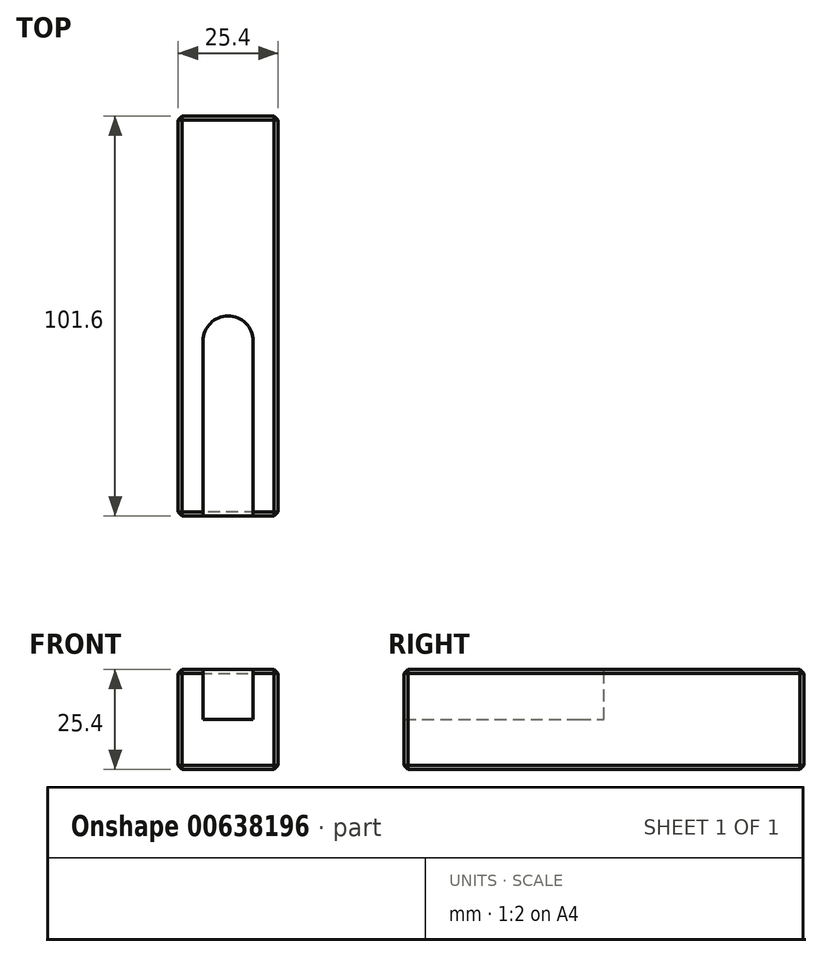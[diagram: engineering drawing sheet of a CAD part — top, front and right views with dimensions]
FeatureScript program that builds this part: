
annotation { "Feature Type Name" : "Feature", "Feature Type Description" : "" }
export const myFeature = defineFeature(function(context is Context, id is Id, definition is map)
    precondition{}
    {
        {
            var Q0;
            Q0=qCreatedBy(makeId("Front.planeOp"),FACE);
            var sketch = newSketch(context, id + "F0", { "sketchPlane" : qUnion([Q0])});
            skLineSegment(sketch, "E0.bottom", {"start": v(12.7, -12.7) * mm, "end": v(-12.7, -12.7) * mm});
            skLineSegment(sketch, "E0.top", {"start": v(12.7, 12.7) * mm, "end": v(-12.7, 12.7) * mm});
            skLineSegment(sketch, "E0.left", {"start": v(12.7, -12.7) * mm, "end": v(12.7, 12.7) * mm});
            skLineSegment(sketch, "E0.right", {"start": v(-12.7, -12.7) * mm, "end": v(-12.7, 12.7) * mm});
            skPoint(sketch, "E0.middle", {"position": v(0, 0) * mm});
            skSolve(sketch);
        }
        {
            var Q0;
            Q0=makeQuery(id+"F0.imprint","IMPRINT",FACE,{"disambiguationData":[TD([[makeQuery(id+"F0.imprint","IMPRINT",EDGE,{"derivedFrom":sQuery(id+"F0.wireOp",EDGE,"E0.bottom")}),-1.0]])]});
            extrude(context, id + "F1", {"entities" : qUnion([Q0]), "endBound" : BoundingType.SYMMETRIC, "depth" : (25.4 * 4) * mm, "offsetDistance" : 25 * mm});
        }
        {
            var Q0;
            Q0=makeQuery(id+"F1.opExtrude","SWEPT_FACE",FACE,{"disambiguationData":[OSD([sQuery(id+"F0.wireOp",EDGE,"E0.top")])]});
            var sketch = newSketch(context, id + "F2", { "sketchPlane" : qUnion([Q0])});
            skLineSegment(sketch, "E1.bottom", {"start": v(-6.35, -50.8) * mm, "end": v(6.35, -50.8) * mm});
            skLineSegment(sketch, "E1.left", {"start": v(-6.35, -50.8) * mm, "end": v(-6.35, -6.35) * mm});
            skLineSegment(sketch, "E1.right", {"start": v(6.35, -50.8) * mm, "end": v(6.35, -6.35) * mm});
            skArc(sketch, "E2", {"start": v(6.35, -6.35) * mm, "mid": v(0, 0) * mm, "end": v(-6.35, -6.35) * mm});
            skSolve(sketch);
        }
        {
            var Q0;
            Q0=makeQuery(id+"F2.imprint","IMPRINT",FACE,{"disambiguationData":[TD([[makeQuery(id+"F2.imprint","IMPRINT",EDGE,{"derivedFrom":sQuery(id+"F2.wireOp",EDGE,"E1.bottom")}),-1.0]])]});
            extrude(context, id + "F3", {"entities" : qUnion([Q0]), "operationType" : NewBodyOperationType.REMOVE, "oppositeDirection" : true, "depth" : (25.4 / 2) * mm, "offsetDistance" : 25 * mm});
        }
        {
            var Q0;
            Q0=makeQuery(id+"F1.opExtrude","SWEPT_FACE",FACE,{"disambiguationData":[OSD([sQuery(id+"F0.wireOp",EDGE,"E0.left")])]});
            var Q1;
            Q1=makeQuery(id+"F1.opExtrude","CAP_FACE",FACE,{"disambiguationData":[OSD([sQuery(id+"F0.wireOp",EDGE,"E0.bottom"),sQuery(id+"F0.wireOp",EDGE,"E0.top"),sQuery(id+"F0.wireOp",EDGE,"E0.left"),sQuery(id+"F0.wireOp",EDGE,"E0.right")])],"isStart":true});
            var Q2;
            Q2=makeQuery(id+"F1.opExtrude","SWEPT_FACE",FACE,{"disambiguationData":[OSD([sQuery(id+"F0.wireOp",EDGE,"E0.right")])]});
            var Q3;
            Q3=makeQuery(id+"F1.opExtrude","SWEPT_FACE",FACE,{"disambiguationData":[OSD([sQuery(id+"F0.wireOp",EDGE,"E0.bottom")])]});
            var Q4;
            {var subQ0=sQuery(id+"F0.wireOp",EDGE,"E0.right");var subQ1=sQuery(id+"F0.wireOp",EDGE,"E0.top");Q4=makeQuery(id+"F3.boolean.opBoolean","SPLIT",EDGE,{"disambiguationData":[TD([makeQuery(id+"F1.opExtrude","SWEPT_FACE",FACE,{"disambiguationData":[OSD([subQ0])]})])],"derivedFrom":makeQuery(id+"F1.opExtrude","CAP_EDGE",EDGE,{"disambiguationData":[OSD([subQ1])],"isStart":false})});}
            var Q5;
            {var subQ0=sQuery(id+"F0.wireOp",EDGE,"E0.left");var subQ1=sQuery(id+"F0.wireOp",EDGE,"E0.top");Q5=makeQuery(id+"F3.boolean.opBoolean","SPLIT",EDGE,{"disambiguationData":[TD([makeQuery(id+"F1.opExtrude","SWEPT_FACE",FACE,{"disambiguationData":[OSD([subQ0])]})])],"derivedFrom":makeQuery(id+"F1.opExtrude","CAP_EDGE",EDGE,{"disambiguationData":[OSD([subQ1])],"isStart":false})});}
            chamfer(context, id + "F4", {"entities" : qUnion([Q0, Q1, Q2, Q3, Q4, Q5]), "width" : 1 * mm, "tangentPropagation" : true});
        }
    });
